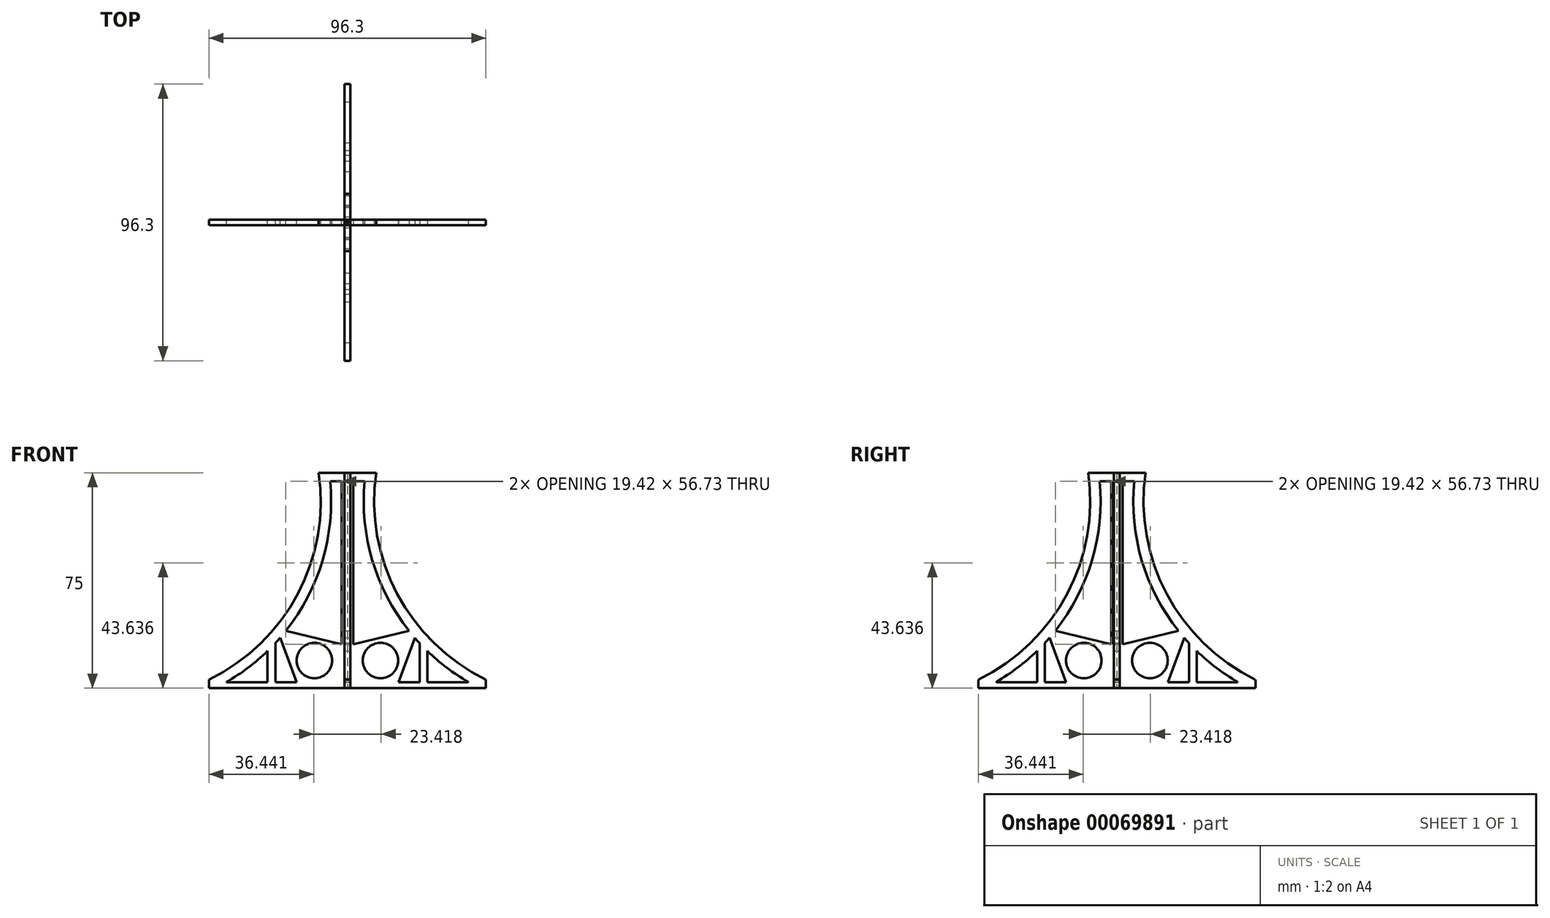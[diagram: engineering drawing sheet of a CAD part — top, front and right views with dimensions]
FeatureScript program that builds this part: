
annotation { "Feature Type Name" : "Feature", "Feature Type Description" : "" }
export const myFeature = defineFeature(function(context is Context, id is Id, definition is map)
    precondition{}
    {
        {
            var Q0;
            Q0=qCreatedBy(makeId("Right.planeOp"),FACE);
            var sketch = newSketch(context, id + "F0", { "sketchPlane" : qUnion([Q0])});
            skLineSegment(sketch, "E0", {"start": v(-10, 75) * mm, "end": v(0, 75) * mm});
            skLineSegment(sketch, "E1", {"start": v(0, 75) * mm, "end": v(0, 0) * mm});
            skLineSegment(sketch, "E2", {"start": v(0, 0) * mm, "end": v(-48.15, 0) * mm});
            skLineSegment(sketch, "E3", {"start": v(-48.15, 0) * mm, "end": v(-48.15, 3) * mm});
            skLineSegment(sketch, "E4", {"start": v(-2, 72) * mm, "end": v(-2, 2) * mm});
            skLineSegment(sketch, "E5", {"start": v(-2, 2) * mm, "end": v(-9.1, 2) * mm});
            skLineSegment(sketch, "E6", {"start": v(-2, 72) * mm, "end": v(-6, 72) * mm});
            skLineSegment(sketch, "E7", {"start": v(-42, 2) * mm, "end": v(-42, 2.18) * mm});
            skLineSegment(sketch, "E8.top", {"start": v(-25.08, 2) * mm, "end": v(-27.76, 2) * mm});
            skLineSegment(sketch, "E8.left", {"start": v(-25.08, 15.65) * mm, "end": v(-25.08, 2) * mm});
            skLineSegment(sketch, "E8.right", {"start": v(-27.76, 12.91) * mm, "end": v(-27.76, 2) * mm});
            skLineSegment(sketch, "E9.top", {"start": v(-12.03, 2) * mm, "end": v(-9.1, 2) * mm});
            skLineSegment(sketch, "E10.top", {"start": v(-17.72, 2) * mm, "end": v(-5.55, 2) * mm});
            skLineSegment(sketch, "E10.right", {"start": v(-23.43, 17.5) * mm, "end": v(-17.72, 2) * mm});
            skPoint(sketch, "E11.firstSnap0", {"position": v(-12, 15.27) * mm});
            skLineSegment(sketch, "E11.bottom", {"start": v(-21.42, 19.92) * mm, "end": v(-2, 15.27) * mm});
            skPoint(sketch, "E12.orphan", {"position": v(-2, 15.27) * mm});
            skLineSegment(sketch, "E13.trimOffspring", {"start": v(-12.03, 2) * mm, "end": v(-42, 2) * mm});
            skArc(sketch, "E14", {"start": v(-48.15, 3) * mm, "mid": v(-17.31, 32.77) * mm, "end": v(-10, 75) * mm});
            skArc(sketch, "E15", {"start": v(-42, 2.18) * mm, "mid": v(-34.55, 7.1) * mm, "end": v(-27.76, 12.91) * mm});
            skArc(sketch, "E16.trimOffspring", {"start": v(-21.42, 19.92) * mm, "mid": v(-8.65, 44.46) * mm, "end": v(-6, 72) * mm});
            skArc(sketch, "E17.trimOffspring", {"start": v(-25.08, 15.65) * mm, "mid": v(-24.25, 16.57) * mm, "end": v(-23.43, 17.5) * mm});
            skCircle(sketch, "E18", {"center": v(-11.5, 9.6) * mm, "radius": 6.18 * mm});
            skSolve(sketch);
        }
        {
            var Q0;
            Q0=qSketchRegion(id+"F0",true);
            extrude(context, id + "F1", {"entities" : qUnion([Q0]), "depth" : 1 * mm, "hasSecondDirection" : true, "secondDirectionOppositeDirection" : true, "secondDirectionDepth" : 1 * mm});
        }
        {
            var Q0;
            Q0=qCreatedBy(makeId("Right.planeOp"),FACE);
            var sketch = newSketch(context, id + "F2", { "sketchPlane" : qUnion([Q0])});
            skLineSegment(sketch, "E19", {"start": v(0, 81) * mm, "end": v(0, -28.5) * mm, "construction": true});
            skSolve(sketch);
        }
        {
            var Q0;
            Q0=makeQuery(id+"F1.opExtrude","SWEPT_BODY",BODY,{"disambiguationData":[OSD([sQuery(id+"F0.wireOp",EDGE,"E0"),sQuery(id+"F0.wireOp",EDGE,"E1"),sQuery(id+"F0.wireOp",EDGE,"E2"),sQuery(id+"F0.wireOp",EDGE,"E3"),sQuery(id+"F0.wireOp",EDGE,"ba3e6201-bb00-4176-be12-0bcf97df4df2"),sQuery(id+"F0.wireOp",EDGE,"E4"),sQuery(id+"F0.wireOp",EDGE,"E5"),sQuery(id+"F0.wireOp",EDGE,"E6"),sQuery(id+"F0.wireOp",EDGE,"E7"),sQuery(id+"F0.wireOp",EDGE,"973229ff-babc-457a-ac66-6eeaf75bea45")])]});
            var Q1;
            Q1=sQuery(id+"F2.wireOp",EDGE,"E19");
            circularPattern(context, id + "F3", {"entities" : qUnion([Q0]), "axis" : qUnion([Q1]), "angle" : 90 * degree, "instanceCount" : round(4)});
        }
    });
